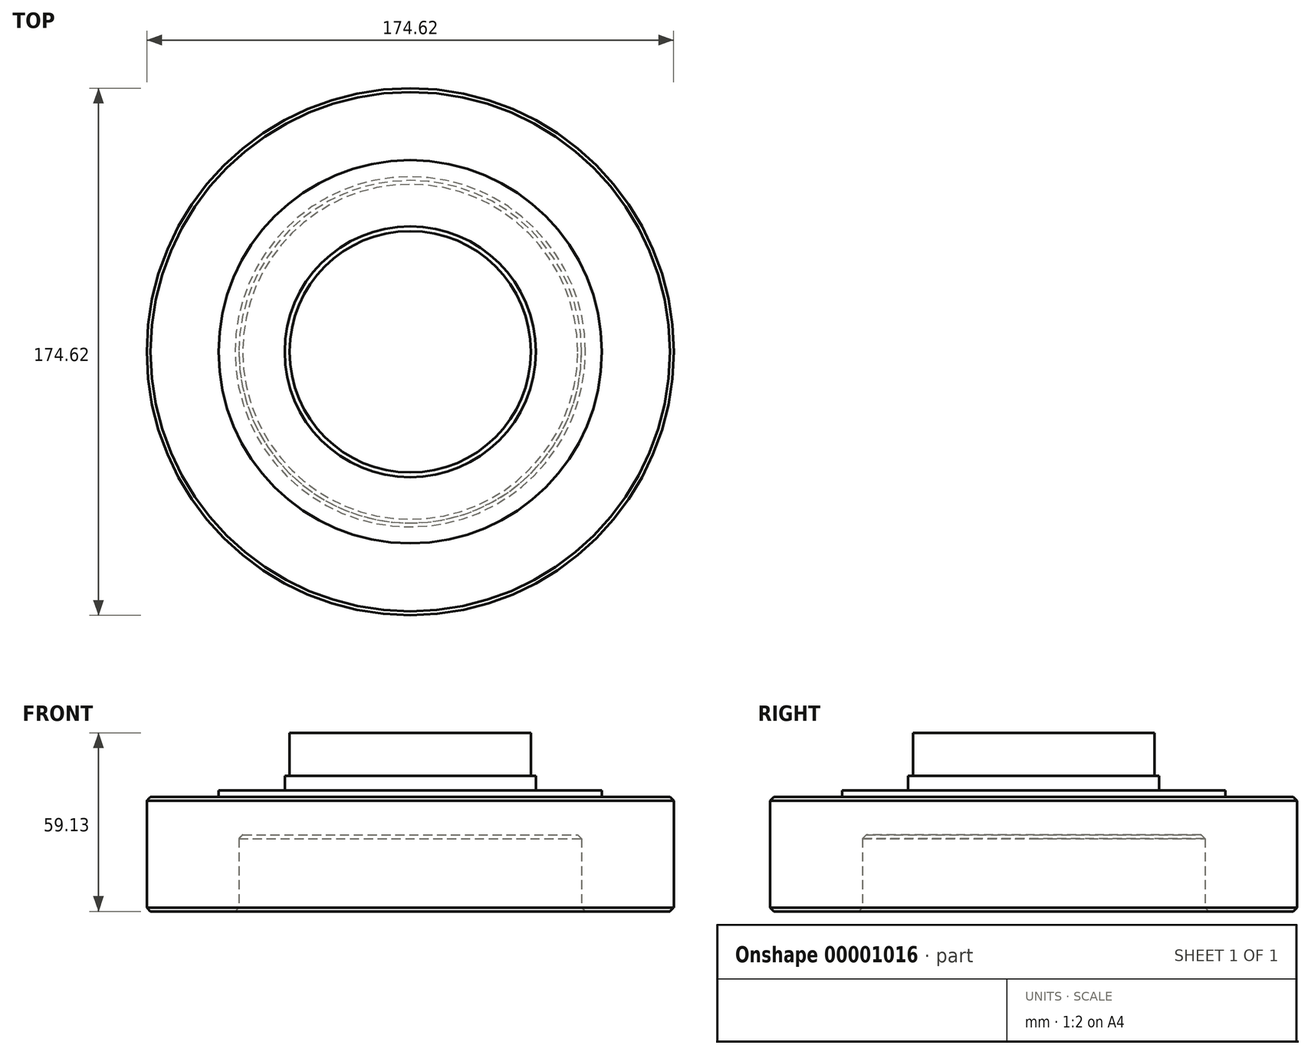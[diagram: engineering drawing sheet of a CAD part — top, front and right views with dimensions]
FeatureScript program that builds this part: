
annotation { "Feature Type Name" : "Feature", "Feature Type Description" : "" }
export const myFeature = defineFeature(function(context is Context, id is Id, definition is map)
    precondition{}
    {
        {
            var Q0;
            Q0=qCreatedBy(makeId("Right.planeOp"),FACE);
            var sketch = newSketch(context, id + "F0", { "sketchPlane" : qUnion([Q0])});
            skLineSegment(sketch, "E0", {"start": v(0, 0) * mm, "end": v(0, 116.91) * mm, "construction": true});
            skLineSegment(sketch, "E1", {"start": v(0, 25.4) * mm, "end": v(0, 59.13) * mm});
            skLineSegment(sketch, "E2", {"start": v(0, 59.13) * mm, "end": v(-40, 59.13) * mm});
            skLineSegment(sketch, "E3", {"start": v(-40, 59.13) * mm, "end": v(-40, 44.9) * mm});
            skLineSegment(sketch, "E4", {"start": v(-63.5, 37.95) * mm, "end": v(-87.31, 37.95) * mm});
            skLineSegment(sketch, "E5", {"start": v(-87.31, 37.95) * mm, "end": v(-87.31, 0) * mm});
            skLineSegment(sketch, "E6", {"start": v(-87.31, 0) * mm, "end": v(-56.77, 0) * mm});
            skLineSegment(sketch, "E7.top", {"start": v(0, 25.4) * mm, "end": v(-56.77, 25.4) * mm});
            skLineSegment(sketch, "E7.right", {"start": v(-56.77, 0) * mm, "end": v(-56.77, 25.4) * mm});
            skLineSegment(sketch, "E8", {"start": v(-63.5, 37.95) * mm, "end": v(-63.5, 40.1) * mm});
            skLineSegment(sketch, "E9", {"start": v(-63.5, 40.1) * mm, "end": v(-41.6, 40.1) * mm});
            skLineSegment(sketch, "E10.top", {"start": v(-40, 44.9) * mm, "end": v(-41.6, 44.9) * mm});
            skLineSegment(sketch, "E10.right", {"start": v(-41.6, 40.1) * mm, "end": v(-41.6, 44.9) * mm});
            skSolve(sketch);
        }
        {
            var Q0;
            Q0=makeQuery(id+"F0.imprint","IMPRINT",FACE,{"disambiguationData":[TD([[makeQuery(id+"F0.imprint","IMPRINT",EDGE,{"derivedFrom":sQuery(id+"F0.wireOp",EDGE,"E1")}),1.0]])]});
            var Q1;
            Q1=sQuery(id+"F0.wireOp",EDGE,"E0");
            revolve(context, id + "F1", {"entities" : qUnion([Q0]), "axis" : qUnion([Q1]), "revolveType" : RevolveType.FULL});
        }
        {
            var Q0;
            Q0=makeQuery(id+"F1.opRevolve","SWEPT_EDGE",EDGE,{"disambiguationData":[OSD([sQuery(id+"F0.wireOp",EDGE,"E4"),sQuery(id+"F0.wireOp",EDGE,"E5")])]});
            var Q1;
            Q1=makeQuery(id+"F1.opRevolve","SWEPT_EDGE",EDGE,{"disambiguationData":[OSD([sQuery(id+"F0.wireOp",EDGE,"E5"),sQuery(id+"F0.wireOp",EDGE,"E6")])]});
            var Q2;
            Q2=makeQuery(id+"F1.opRevolve","SWEPT_EDGE",EDGE,{"disambiguationData":[OSD([sQuery(id+"F0.wireOp",EDGE,"E7.top"),sQuery(id+"F0.wireOp",EDGE,"E7.right")])]});
            var Q3;
            Q3=makeQuery(id+"F1.opRevolve","SWEPT_EDGE",EDGE,{"disambiguationData":[OSD([sQuery(id+"F0.wireOp",EDGE,"E6"),sQuery(id+"F0.wireOp",EDGE,"E7.right")])]});
            chamfer(context, id + "F2", {"entities" : qUnion([Q0, Q1, Q2, Q3]), "width" : 1.27 * mm, "tangentPropagation" : true});
        }
    });
